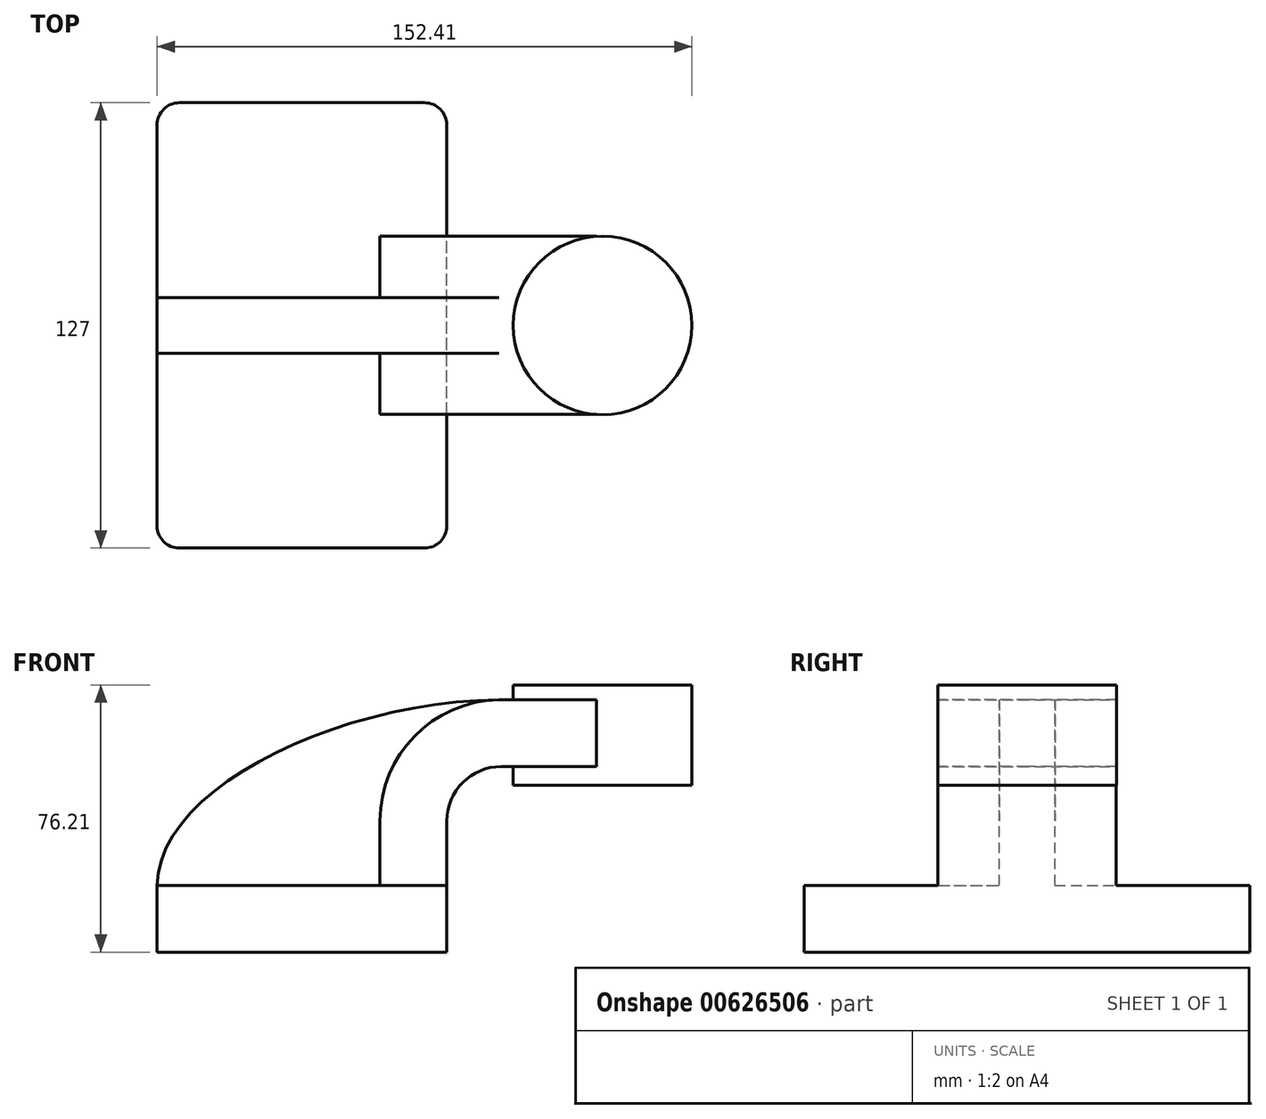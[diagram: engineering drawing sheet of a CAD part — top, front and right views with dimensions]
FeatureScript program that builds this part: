
annotation { "Feature Type Name" : "Feature", "Feature Type Description" : "" }
export const myFeature = defineFeature(function(context is Context, id is Id, definition is map)
    precondition{}
    {
        {
            var Q0;
            Q0=qCreatedBy(makeId("Front.planeOp"),FACE);
            var sketch = newSketch(context, id + "F0", { "sketchPlane" : qUnion([Q0])});
            skLineSegment(sketch, "E0.bottom", {"start": v(-41.28, -9.53) * mm, "end": v(41.28, -9.53) * mm});
            skLineSegment(sketch, "E0.top", {"start": v(-41.28, 9.53) * mm, "end": v(41.28, 9.53) * mm});
            skLineSegment(sketch, "E0.left", {"start": v(-41.28, -9.53) * mm, "end": v(-41.28, 9.53) * mm});
            skLineSegment(sketch, "E0.right", {"start": v(41.28, -9.53) * mm, "end": v(41.28, 9.53) * mm});
            skPoint(sketch, "E0.middle", {"position": v(0, 0) * mm});
            skLineSegment(sketch, "E1.bottom", {"start": v(60.33, 38.1) * mm, "end": v(111.12, 38.1) * mm});
            skLineSegment(sketch, "E1.top", {"start": v(60.33, 66.67) * mm, "end": v(111.12, 66.67) * mm});
            skLineSegment(sketch, "E1.left", {"start": v(60.33, 38.1) * mm, "end": v(60.33, 66.67) * mm});
            skLineSegment(sketch, "E1.right", {"start": v(111.12, 38.1) * mm, "end": v(111.12, 66.67) * mm});
            skPoint(sketch, "E1.middle", {"position": v(85.72, 52.39) * mm});
            skLineSegment(sketch, "E2", {"start": v(41.28, 9.53) * mm, "end": v(41.28, 27.9) * mm});
            skArc(sketch, "E3", {"start": v(41.28, 27.9) * mm, "mid": v(45.8, 38.85) * mm, "end": v(56.76, 43.38) * mm});
            skLineSegment(sketch, "E4", {"start": v(56.76, 43.38) * mm, "end": v(85.66, 43.38) * mm});
            skLineSegment(sketch, "E5.0", {"start": v(56.76, 62.43) * mm, "end": v(85.66, 62.43) * mm});
            skArc(sketch, "E5.1", {"start": v(22.23, 27.9) * mm, "mid": v(32.34, 52.32) * mm, "end": v(56.76, 62.43) * mm});
            skLineSegment(sketch, "E5.2", {"start": v(22.23, 9.53) * mm, "end": v(22.23, 27.9) * mm});
            skLineSegment(sketch, "E6", {"start": v(85.66, 38.1) * mm, "end": v(85.66, 66.67) * mm});
            skFitSpline(sketch, "E7", {"points": [v(-41.28, 9.53) * mm, v(56.76, 62.43) * mm], "startDerivative": vector(0.8, 83.17) * mm, "endDerivative": vector(139.51, 1.05) * mm});
            skSolve(sketch);
        }
        {
            var Q0;
            Q0=makeQuery(id+"F0.imprint","IMPRINT",FACE,{"disambiguationData":[TD([[makeQuery(id+"F0.imprint","IMPRINT",EDGE,{"derivedFrom":sQuery(id+"F0.wireOp",EDGE,"E0.bottom")}),1.0]])]});
            extrude(context, id + "F1", {"entities" : qUnion([Q0]), "endBound" : BoundingType.SYMMETRIC, "depth" : 127 * mm, "offsetDistance" : 25.4 * mm});
        }
        {
            var Q0;
            {var subQ1=sQuery(id+"F0.wireOp",EDGE,"E2");Q0=makeQuery(id+"F0.imprint","IMPRINT",FACE,{"disambiguationData":[TD([[makeQuery(id+"F0.imprint","IMPRINT",EDGE,{"derivedFrom":subQ1}),1.0]])]});}
            extrude(context, id + "F2", {"entities" : qUnion([Q0]), "operationType" : NewBodyOperationType.ADD, "endBound" : BoundingType.SYMMETRIC, "depth" : 50.8 * mm, "offsetDistance" : 25.4 * mm});
        }
        {
            var Q0;
            {var subQ3=sQuery(id+"F0.wireOp",EDGE,"E5.2");Q0=makeQuery(id+"F0.imprint","IMPRINT",FACE,{"disambiguationData":[TD([[makeQuery(id+"F0.imprint","IMPRINT",EDGE,{"derivedFrom":subQ3}),1.0]])]});}
            extrude(context, id + "F3", {"entities" : qUnion([Q0]), "operationType" : NewBodyOperationType.ADD, "endBound" : BoundingType.SYMMETRIC, "depth" : 15.88 * mm, "offsetDistance" : 25.4 * mm});
        }
        {
            var Q0;
            {var subQ0=sQuery(id+"F0.wireOp",EDGE,"E4");var subQ1=sQuery(id+"F0.wireOp",EDGE,"E1.left");var subQ2=makeQuery(id+"F0.imprint","INTERSECT",VERTEX,{"derivedFrom":[subQ1,subQ0]});Q0=makeQuery(id+"F0.imprint","IMPRINT",FACE,{"disambiguationData":[TD([[makeQuery(id+"F0.imprint","IMPRINT",EDGE,{"disambiguationData":[TD([[subQ2,-1.0]])],"derivedFrom":subQ1}),-1.0]])]});}
            extrude(context, id + "F4", {"entities" : qUnion([Q0]), "operationType" : NewBodyOperationType.ADD, "endBound" : BoundingType.SYMMETRIC, "depth" : 50.8 * mm, "offsetDistance" : 25.4 * mm});
        }
        {
            var Q0;
            {var subQ4=sQuery(id+"F0.wireOp",EDGE,"E1.right");Q0=makeQuery(id+"F0.imprint","IMPRINT",FACE,{"disambiguationData":[TD([[makeQuery(id+"F0.imprint","IMPRINT",EDGE,{"derivedFrom":subQ4}),1.0]])]});}
            var Q1;
            Q1=sQuery(id+"F0.wireOp",EDGE,"E6");
            revolve(context, id + "F5", {"operationType" : NewBodyOperationType.ADD, "entities" : qUnion([Q0]), "axis" : qUnion([Q1]), "revolveType" : RevolveType.FULL});
        }
        {
            var Q0;
            Q0=makeQuery(id+"F1.opExtrude","CAP_EDGE",EDGE,{"disambiguationData":[OSD([sQuery(id+"F0.wireOp",EDGE,"E0.right")])],"isStart":false});
            var Q1;
            Q1=makeQuery(id+"F1.opExtrude","CAP_EDGE",EDGE,{"disambiguationData":[OSD([sQuery(id+"F0.wireOp",EDGE,"E0.left")])],"isStart":false});
            var Q2;
            Q2=makeQuery(id+"F1.opExtrude","CAP_EDGE",EDGE,{"disambiguationData":[OSD([sQuery(id+"F0.wireOp",EDGE,"E0.right")])],"isStart":true});
            var Q3;
            Q3=makeQuery(id+"F1.opExtrude","CAP_EDGE",EDGE,{"disambiguationData":[OSD([sQuery(id+"F0.wireOp",EDGE,"E0.left")])],"isStart":true});
            fillet(context, id + "F6", {"entities" : qUnion([Q0, Q1, Q2, Q3]), "radius" : 6.35 * mm, "tangentPropagation" : true, "allowEdgeOverflow" : false});
        }
    });
